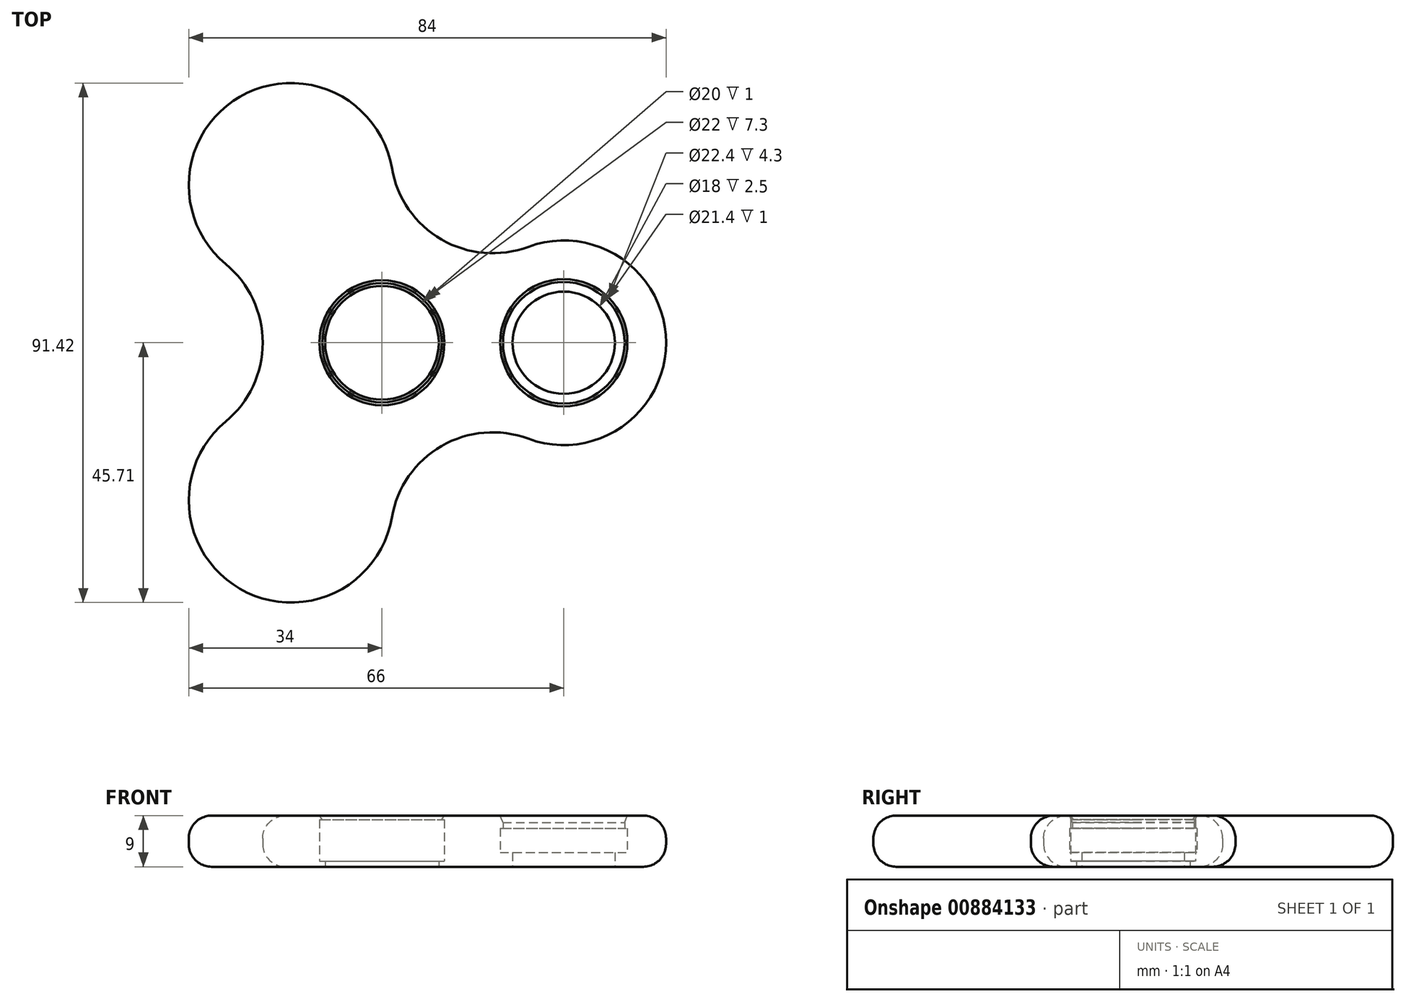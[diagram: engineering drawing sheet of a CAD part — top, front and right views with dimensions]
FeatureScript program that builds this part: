
annotation { "Feature Type Name" : "Feature", "Feature Type Description" : "" }
export const myFeature = defineFeature(function(context is Context, id is Id, definition is map)
    precondition{}
    {
        {
            var Q0;
            Q0=qCreatedBy(makeId("Top.planeOp"),FACE);
            var sketch = newSketch(context, id + "F0", { "sketchPlane" : qUnion([Q0])});
            skLineSegment(sketch, "E0", {"start": v(0, 0) * mm, "end": v(32, 0) * mm, "construction": true});
            skCircle(sketch, "E1", {"center": v(0, 0) * mm, "radius": 32 * mm, "construction": true});
            skLineSegment(sketch, "E2", {"start": v(0, 0) * mm, "end": v(-16, 27.71) * mm, "construction": true});
            skLineSegment(sketch, "E3", {"start": v(0, 0) * mm, "end": v(-16, -27.71) * mm, "construction": true});
            skArc(sketch, "E4", {"start": v(25.74, -16.88) * mm, "mid": v(50, 0) * mm, "end": v(25.74, 16.88) * mm});
            skArc(sketch, "E5", {"start": v(1.74, 30.73) * mm, "mid": v(-25, 43.3) * mm, "end": v(-27.49, 13.86) * mm});
            skArc(sketch, "E6", {"start": v(-27.49, -13.86) * mm, "mid": v(-25, -43.3) * mm, "end": v(1.74, -30.73) * mm});
            skArc(sketch, "E7", {"start": v(1.74, 30.73) * mm, "mid": v(10.49, 18.17) * mm, "end": v(25.74, 16.88) * mm});
            skArc(sketch, "E8.1.0", {"start": v(-27.49, -13.86) * mm, "mid": v(-20.98, 0) * mm, "end": v(-27.49, 13.86) * mm});
            skArc(sketch, "E8.2.0", {"start": v(25.74, -16.88) * mm, "mid": v(10.49, -18.17) * mm, "end": v(1.74, -30.73) * mm});
            skSolve(sketch);
        }
        {
            var Q0;
            Q0=qSketchRegion(id+"F0",true);
            extrude(context, id + "F1", {"entities" : qUnion([Q0]), "depth" : 9 * mm, "offsetDistance" : 25 * mm});
        }
        {
            var Q0;
            Q0=qCreatedBy(makeId("Right.planeOp"),FACE);
            var sketch = newSketch(context, id + "F2", { "sketchPlane" : qUnion([Q0])});
            skLineSegment(sketch, "E9", {"start": v(0, 0) * mm, "end": v(0, 9) * mm});
            skLineSegment(sketch, "E10", {"start": v(0, 9) * mm, "end": v(11, 9) * mm});
            skLineSegment(sketch, "E11", {"start": v(11, 9) * mm, "end": v(10.5, 8.3) * mm});
            skLineSegment(sketch, "E12", {"start": v(10.5, 8.3) * mm, "end": v(11, 8.3) * mm});
            skLineSegment(sketch, "E13", {"start": v(11, 8.3) * mm, "end": v(11, 1) * mm});
            skLineSegment(sketch, "E14", {"start": v(11, 1) * mm, "end": v(10, 1) * mm});
            skLineSegment(sketch, "E15", {"start": v(10, 1) * mm, "end": v(10, 0) * mm});
            skLineSegment(sketch, "E16", {"start": v(10, 0) * mm, "end": v(0, 0) * mm});
            skLineSegment(sketch, "E17", {"start": v(0, 17.58) * mm, "end": v(0, -10.03) * mm, "construction": true});
            skSolve(sketch);
        }
        {
            var Q0;
            Q0=qSketchRegion(id+"F2",true);
            var Q1;
            Q1=sQuery(id+"F2.wireOp",EDGE,"E17");
            revolve(context, id + "F3", {"operationType" : NewBodyOperationType.REMOVE, "surfaceOperationType" : NewSurfaceOperationType.NEW, "entities" : qUnion([Q0]), "axis" : qUnion([Q1]), "revolveType" : RevolveType.FULL, "oppositeDirection" : true});
        }
        {
            var Q0;
            Q0=qCreatedBy(makeId("Front.planeOp"),FACE);
            var sketch = newSketch(context, id + "F4", { "sketchPlane" : qUnion([Q0])});
            skLineSegment(sketch, "E18", {"start": v(32, 31.94) * mm, "end": v(32, -19.35) * mm, "construction": true});
            skLineSegment(sketch, "E19", {"start": v(32, 0) * mm, "end": v(32, 9) * mm});
            skLineSegment(sketch, "E20", {"start": v(32, 9) * mm, "end": v(20.8, 9) * mm});
            skLineSegment(sketch, "E21", {"start": v(21.3, 6.8) * mm, "end": v(20.8, 6.8) * mm});
            skLineSegment(sketch, "E22", {"start": v(20.8, 6.8) * mm, "end": v(20.8, 2.5) * mm});
            skLineSegment(sketch, "E23", {"start": v(20.8, 2.5) * mm, "end": v(23, 2.5) * mm});
            skLineSegment(sketch, "E24", {"start": v(23, 2.5) * mm, "end": v(23, 0) * mm});
            skLineSegment(sketch, "E25", {"start": v(23, 0) * mm, "end": v(32, 0) * mm});
            skLineSegment(sketch, "E26", {"start": v(21.3, 6.8) * mm, "end": v(21.3, 7.8) * mm});
            skLineSegment(sketch, "E27", {"start": v(21.3, 7.8) * mm, "end": v(20.8, 9) * mm});
            skSolve(sketch);
        }
        {
            var Q0;
            Q0=qSketchRegion(id+"F4",true);
            var Q1;
            Q1=sQuery(id+"F4.wireOp",EDGE,"E18");
            revolve(context, id + "F5", {"operationType" : NewBodyOperationType.REMOVE, "surfaceOperationType" : NewSurfaceOperationType.NEW, "entities" : qUnion([Q0]), "axis" : qUnion([Q1]), "revolveType" : RevolveType.FULL, "oppositeDirection" : true});
        }
        {
            var Q0;
            Q0=makeQuery(id+"F1.opExtrude","CAP_EDGE",EDGE,{"disambiguationData":[OSD([sQuery(id+"F0.wireOp",EDGE,"E7")])],"isStart":false});
            var Q1;
            Q1=makeQuery(id+"F1.opExtrude","CAP_EDGE",EDGE,{"disambiguationData":[OSD([sQuery(id+"F0.wireOp",EDGE,"E7")])],"isStart":true});
            fillet(context, id + "F6", {"entities" : qUnion([Q0, Q1]), "radius" : 4 * mm, "tangentPropagation" : true, "allowEdgeOverflow" : false});
        }
    });
